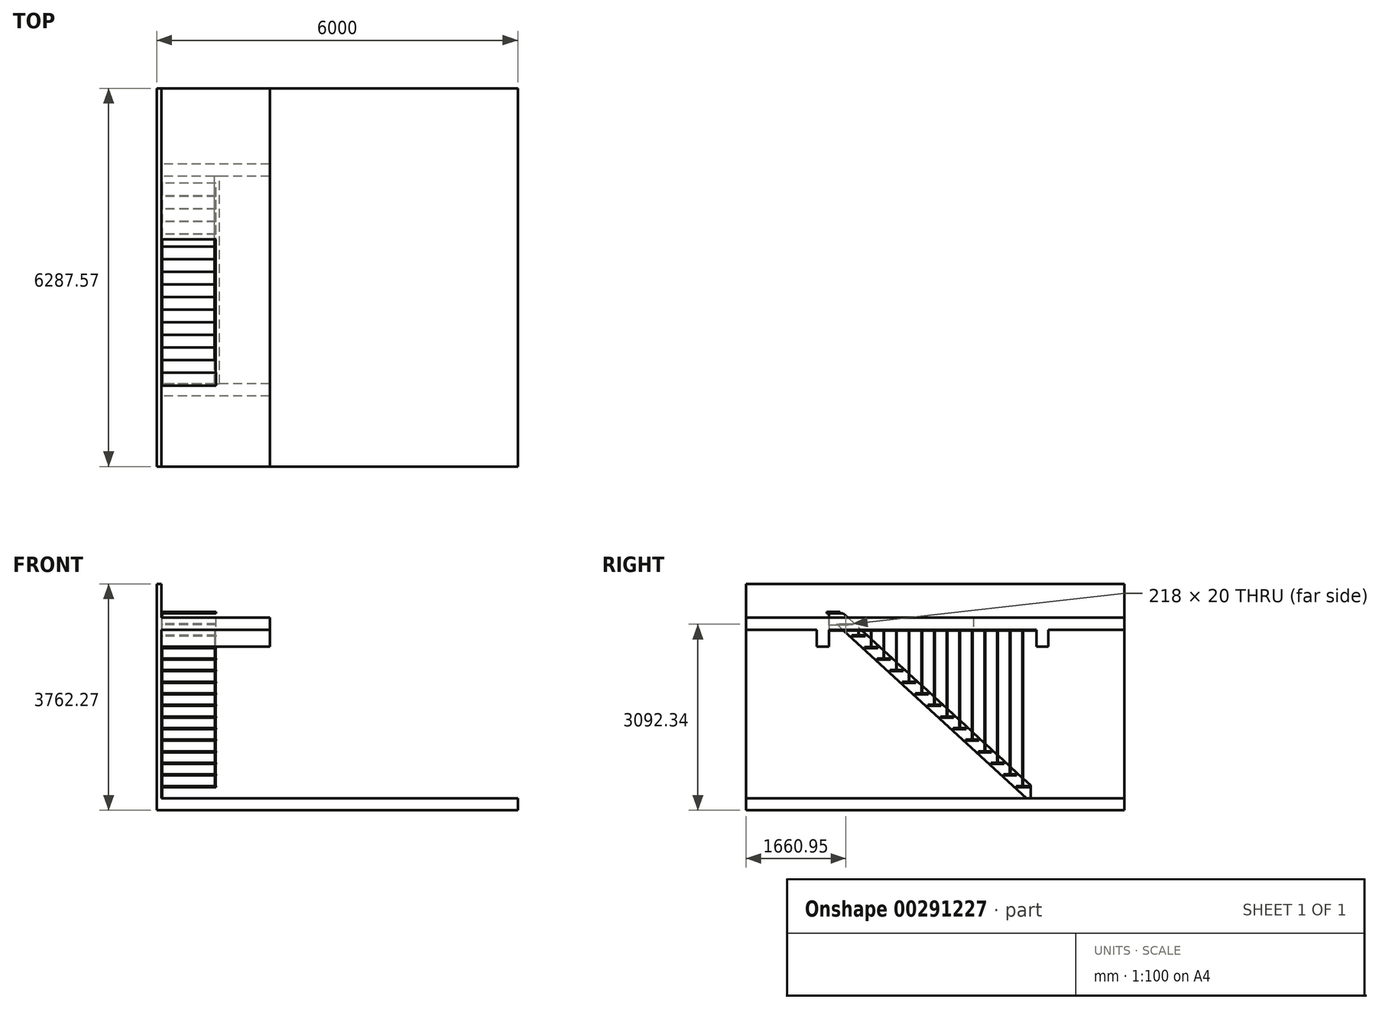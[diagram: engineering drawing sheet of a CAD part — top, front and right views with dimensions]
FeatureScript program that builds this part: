
annotation { "Feature Type Name" : "Feature", "Feature Type Description" : "" }
export const myFeature = defineFeature(function(context is Context, id is Id, definition is map)
    precondition{}
    {
        {
            var Q0;
            Q0=qCreatedBy(makeId("Right.planeOp"),FACE);
            var sketch = newSketch(context, id + "F0", { "sketchPlane" : qUnion([Q0])});
            skLineSegment(sketch, "E0", {"start": v(-3201.03, 2875.04) * mm, "end": v(-3352.23, 2875.04) * mm});
            skLineSegment(sketch, "E1", {"start": v(-3352.23, 2875.04) * mm, "end": v(-3352.23, 3075.04) * mm});
            skLineSegment(sketch, "E2", {"start": v(-3352.23, 3075.04) * mm, "end": v(-3115.13, 3075.04) * mm});
            skLineSegment(sketch, "E3", {"start": v(-3115.13, 3075.04) * mm, "end": v(0, 214.6) * mm});
            skLineSegment(sketch, "E4", {"start": v(0, 214.6) * mm, "end": v(0, 0) * mm});
            skLineSegment(sketch, "E5", {"start": v(0, 0) * mm, "end": v(-70, 0) * mm});
            skLineSegment(sketch, "E6", {"start": v(-70, 0) * mm, "end": v(-3201.03, 2875.04) * mm});
            skSolve(sketch);
        }
        {
            var Q0;
            Q0 = qSketchRegion(id + "F0", true);
            extrude(context, id + "F1", {"entities" : qUnion([Q0]), "depth" : 10 * mm});
        }
        {
            var Q0;
            Q0=qCreatedBy(makeId("Right.planeOp"),FACE);
            var sketch = newSketch(context, id + "F2", { "sketchPlane" : qUnion([Q0])});
            skLineSegment(sketch, "E7.bottom", {"start": v(-4728.97, 3562.27) * mm, "end": v(1558.6, 3562.27) * mm});
            skLineSegment(sketch, "E7.top", {"start": v(-4728.97, 0) * mm, "end": v(1558.6, 0) * mm});
            skLineSegment(sketch, "E7.left", {"start": v(-4728.97, 3562.27) * mm, "end": v(-4728.97, 0) * mm});
            skLineSegment(sketch, "E7.right", {"start": v(1558.6, 3562.27) * mm, "end": v(1558.6, 0) * mm});
            skSolve(sketch);
        }
        {
            var Q0;
            Q0 = qSketchRegion(id + "F2", true);
            extrude(context, id + "F3", {"entities" : qUnion([Q0]), "operationType" : NewBodyOperationType.ADD, "oppositeDirection" : true, "depth" : 80 * mm});
        }
        {
            var Q0;
            Q0=makeQuery(id+"F1.opExtrude","CAP_FACE",FACE,{"disambiguationData":[OSD([sQuery(id+"F0.wireOp",EDGE,"E0"),sQuery(id+"F0.wireOp",EDGE,"E1"),sQuery(id+"F0.wireOp",EDGE,"E2"),sQuery(id+"F0.wireOp",EDGE,"E3"),sQuery(id+"F0.wireOp",EDGE,"E4"),sQuery(id+"F0.wireOp",EDGE,"E5"),sQuery(id+"F0.wireOp",EDGE,"E6")])],"isStart":false});
            var sketch = newSketch(context, id + "F4", { "sketchPlane" : qUnion([Q0])});
            skLineSegment(sketch, "E8", {"start": v(0, 214.6) * mm, "end": v(-138.93, 63.3) * mm, "construction": true});
            skLineSegment(sketch, "E9", {"start": v(-69.47, 138.95) * mm, "end": v(-3158.58, 2975.5) * mm, "construction": true});
            skSolve(sketch);
        }
        {
            var Q0;
            Q0=makeQuery(id+"F4.imprint","IMPRINT",FACE,{"disambiguationData":[TD([[makeQuery(id+"F4.imprint","IMPRINT",EDGE,{"derivedFrom":makeQuery(id+"F1.opExtrude","CAP_EDGE",EDGE,{"disambiguationData":[OSD([sQuery(id+"F0.wireOp",EDGE,"E0")])],"isStart":false})}),-1.0]])]});
            var sketch = newSketch(context, id + "F5", { "sketchPlane" : qUnion([Q0])});
            skLineSegment(sketch, "E10.bottom", {"start": v(-239.07, 204.6) * mm, "end": v(-21.07, 204.6) * mm});
            skLineSegment(sketch, "E10.top", {"start": v(-239.07, 184.6) * mm, "end": v(-21.07, 184.6) * mm});
            skLineSegment(sketch, "E10.left", {"start": v(-239.07, 204.6) * mm, "end": v(-239.07, 184.6) * mm});
            skLineSegment(sketch, "E10.right", {"start": v(-21.07, 204.6) * mm, "end": v(-21.07, 184.6) * mm});
            skLineSegment(sketch, "E11", {"start": v(-130.07, 204.6) * mm, "end": v(-130.07, 184.6) * mm, "construction": true});
            skPoint(sketch, "E12", {"position": v(-130.07, 194.6) * mm});
            skPoint(sketch, "E13.0.1.0", {"position": v(-339.93, 387.3) * mm});
            skLineSegment(sketch, "E13.0.1.1", {"start": v(-448.93, 397.3) * mm, "end": v(-230.93, 397.3) * mm});
            skLineSegment(sketch, "E13.0.1.2", {"start": v(-448.93, 397.3) * mm, "end": v(-448.93, 377.3) * mm});
            skLineSegment(sketch, "E13.0.1.3", {"start": v(-448.93, 377.3) * mm, "end": v(-230.93, 377.3) * mm});
            skLineSegment(sketch, "E13.0.1.4", {"start": v(-230.93, 397.3) * mm, "end": v(-230.93, 377.3) * mm});
            skPoint(sketch, "E13.0.2.0", {"position": v(-549.78, 580) * mm});
            skLineSegment(sketch, "E13.0.2.1", {"start": v(-658.78, 590) * mm, "end": v(-440.78, 590) * mm});
            skLineSegment(sketch, "E13.0.2.2", {"start": v(-658.78, 590) * mm, "end": v(-658.78, 570) * mm});
            skLineSegment(sketch, "E13.0.2.3", {"start": v(-658.78, 570) * mm, "end": v(-440.78, 570) * mm});
            skLineSegment(sketch, "E13.0.2.4", {"start": v(-440.78, 590) * mm, "end": v(-440.78, 570) * mm});
            skPoint(sketch, "E13.0.3.0", {"position": v(-759.63, 772.69) * mm});
            skLineSegment(sketch, "E13.0.3.1", {"start": v(-868.63, 782.69) * mm, "end": v(-650.63, 782.69) * mm});
            skLineSegment(sketch, "E13.0.3.2", {"start": v(-868.63, 782.69) * mm, "end": v(-868.63, 762.69) * mm});
            skLineSegment(sketch, "E13.0.3.3", {"start": v(-868.63, 762.69) * mm, "end": v(-650.63, 762.69) * mm});
            skLineSegment(sketch, "E13.0.3.4", {"start": v(-650.63, 782.69) * mm, "end": v(-650.63, 762.69) * mm});
            skPoint(sketch, "E13.0.4.0", {"position": v(-969.49, 965.38) * mm});
            skLineSegment(sketch, "E13.0.4.1", {"start": v(-1078.49, 975.38) * mm, "end": v(-860.49, 975.38) * mm});
            skLineSegment(sketch, "E13.0.4.2", {"start": v(-1078.49, 975.38) * mm, "end": v(-1078.49, 955.38) * mm});
            skLineSegment(sketch, "E13.0.4.3", {"start": v(-1078.49, 955.38) * mm, "end": v(-860.49, 955.38) * mm});
            skLineSegment(sketch, "E13.0.4.4", {"start": v(-860.49, 975.38) * mm, "end": v(-860.49, 955.38) * mm});
            skPoint(sketch, "E13.0.5.0", {"position": v(-1179.34, 1158.08) * mm});
            skLineSegment(sketch, "E13.0.5.1", {"start": v(-1288.34, 1168.08) * mm, "end": v(-1070.34, 1168.08) * mm});
            skLineSegment(sketch, "E13.0.5.2", {"start": v(-1288.34, 1168.08) * mm, "end": v(-1288.34, 1148.08) * mm});
            skLineSegment(sketch, "E13.0.5.3", {"start": v(-1288.34, 1148.08) * mm, "end": v(-1070.34, 1148.08) * mm});
            skLineSegment(sketch, "E13.0.5.4", {"start": v(-1070.34, 1168.08) * mm, "end": v(-1070.34, 1148.08) * mm});
            skPoint(sketch, "E13.0.6.0", {"position": v(-1389.2, 1350.77) * mm});
            skLineSegment(sketch, "E13.0.6.1", {"start": v(-1498.2, 1360.77) * mm, "end": v(-1280.2, 1360.77) * mm});
            skLineSegment(sketch, "E13.0.6.2", {"start": v(-1498.2, 1360.77) * mm, "end": v(-1498.2, 1340.77) * mm});
            skLineSegment(sketch, "E13.0.6.3", {"start": v(-1498.2, 1340.77) * mm, "end": v(-1280.2, 1340.77) * mm});
            skLineSegment(sketch, "E13.0.6.4", {"start": v(-1280.2, 1360.77) * mm, "end": v(-1280.2, 1340.77) * mm});
            skPoint(sketch, "E13.0.7.0", {"position": v(-1599.05, 1543.47) * mm});
            skLineSegment(sketch, "E13.0.7.1", {"start": v(-1708.05, 1553.47) * mm, "end": v(-1490.05, 1553.47) * mm});
            skLineSegment(sketch, "E13.0.7.2", {"start": v(-1708.05, 1553.47) * mm, "end": v(-1708.05, 1533.47) * mm});
            skLineSegment(sketch, "E13.0.7.3", {"start": v(-1708.05, 1533.47) * mm, "end": v(-1490.05, 1533.47) * mm});
            skLineSegment(sketch, "E13.0.7.4", {"start": v(-1490.05, 1553.47) * mm, "end": v(-1490.05, 1533.47) * mm});
            skPoint(sketch, "E13.0.8.0", {"position": v(-1808.9, 1736.17) * mm});
            skLineSegment(sketch, "E13.0.8.1", {"start": v(-1917.9, 1746.17) * mm, "end": v(-1699.9, 1746.17) * mm});
            skLineSegment(sketch, "E13.0.8.2", {"start": v(-1917.9, 1746.17) * mm, "end": v(-1917.9, 1726.17) * mm});
            skLineSegment(sketch, "E13.0.8.3", {"start": v(-1917.9, 1726.17) * mm, "end": v(-1699.9, 1726.17) * mm});
            skLineSegment(sketch, "E13.0.8.4", {"start": v(-1699.9, 1746.17) * mm, "end": v(-1699.9, 1726.17) * mm});
            skPoint(sketch, "E13.0.9.0", {"position": v(-2018.75, 1928.86) * mm});
            skLineSegment(sketch, "E13.0.9.1", {"start": v(-2127.75, 1938.86) * mm, "end": v(-1909.75, 1938.86) * mm});
            skLineSegment(sketch, "E13.0.9.2", {"start": v(-2127.75, 1938.86) * mm, "end": v(-2127.75, 1918.86) * mm});
            skLineSegment(sketch, "E13.0.9.3", {"start": v(-2127.75, 1918.86) * mm, "end": v(-1909.75, 1918.86) * mm});
            skLineSegment(sketch, "E13.0.9.4", {"start": v(-1909.75, 1938.86) * mm, "end": v(-1909.75, 1918.86) * mm});
            skPoint(sketch, "E13.0.10.0", {"position": v(-2228.6, 2121.56) * mm});
            skLineSegment(sketch, "E13.0.10.1", {"start": v(-2337.6, 2131.56) * mm, "end": v(-2119.6, 2131.56) * mm});
            skLineSegment(sketch, "E13.0.10.2", {"start": v(-2337.6, 2131.56) * mm, "end": v(-2337.6, 2111.56) * mm});
            skLineSegment(sketch, "E13.0.10.3", {"start": v(-2337.6, 2111.56) * mm, "end": v(-2119.6, 2111.56) * mm});
            skLineSegment(sketch, "E13.0.10.4", {"start": v(-2119.6, 2131.56) * mm, "end": v(-2119.6, 2111.56) * mm});
            skPoint(sketch, "E13.0.11.0", {"position": v(-2438.46, 2314.25) * mm});
            skLineSegment(sketch, "E13.0.11.1", {"start": v(-2547.46, 2324.25) * mm, "end": v(-2329.46, 2324.25) * mm});
            skLineSegment(sketch, "E13.0.11.2", {"start": v(-2547.46, 2324.25) * mm, "end": v(-2547.46, 2304.25) * mm});
            skLineSegment(sketch, "E13.0.11.3", {"start": v(-2547.46, 2304.25) * mm, "end": v(-2329.46, 2304.25) * mm});
            skLineSegment(sketch, "E13.0.11.4", {"start": v(-2329.46, 2324.25) * mm, "end": v(-2329.46, 2304.25) * mm});
            skPoint(sketch, "E13.0.12.0", {"position": v(-2648.32, 2506.95) * mm});
            skLineSegment(sketch, "E13.0.12.1", {"start": v(-2757.32, 2516.95) * mm, "end": v(-2539.32, 2516.95) * mm});
            skLineSegment(sketch, "E13.0.12.2", {"start": v(-2757.32, 2516.95) * mm, "end": v(-2757.32, 2496.95) * mm});
            skLineSegment(sketch, "E13.0.12.3", {"start": v(-2757.32, 2496.95) * mm, "end": v(-2539.32, 2496.95) * mm});
            skLineSegment(sketch, "E13.0.12.4", {"start": v(-2539.32, 2516.95) * mm, "end": v(-2539.32, 2496.95) * mm});
            skPoint(sketch, "E13.0.13.0", {"position": v(-2858.17, 2699.64) * mm});
            skLineSegment(sketch, "E13.0.13.1", {"start": v(-2967.17, 2709.64) * mm, "end": v(-2749.17, 2709.64) * mm});
            skLineSegment(sketch, "E13.0.13.2", {"start": v(-2967.17, 2709.64) * mm, "end": v(-2967.17, 2689.64) * mm});
            skLineSegment(sketch, "E13.0.13.3", {"start": v(-2967.17, 2689.64) * mm, "end": v(-2749.17, 2689.64) * mm});
            skLineSegment(sketch, "E13.0.13.4", {"start": v(-2749.17, 2709.64) * mm, "end": v(-2749.17, 2689.64) * mm});
            skPoint(sketch, "E13.0.14.0", {"position": v(-3068.02, 2892.34) * mm});
            skLineSegment(sketch, "E13.0.14.1", {"start": v(-3177.02, 2902.34) * mm, "end": v(-2959.02, 2902.34) * mm});
            skLineSegment(sketch, "E13.0.14.2", {"start": v(-3177.02, 2902.34) * mm, "end": v(-3177.02, 2882.34) * mm});
            skLineSegment(sketch, "E13.0.14.3", {"start": v(-3177.02, 2882.34) * mm, "end": v(-2959.02, 2882.34) * mm});
            skLineSegment(sketch, "E13.0.14.4", {"start": v(-2959.02, 2902.34) * mm, "end": v(-2959.02, 2882.34) * mm});
            skPoint(sketch, "E13.0.15.0", {"position": v(-3277.88, 3085.04) * mm});
            skLineSegment(sketch, "E13.0.15.1", {"start": v(-3386.88, 3095.04) * mm, "end": v(-3168.88, 3095.04) * mm});
            skLineSegment(sketch, "E13.0.15.2", {"start": v(-3386.88, 3095.04) * mm, "end": v(-3386.88, 3075.04) * mm});
            skLineSegment(sketch, "E13.0.15.3", {"start": v(-3386.88, 3075.04) * mm, "end": v(-3168.88, 3075.04) * mm});
            skLineSegment(sketch, "E13.0.15.4", {"start": v(-3168.88, 3095.04) * mm, "end": v(-3168.88, 3075.04) * mm});
            skLineSegment(sketch, "E13.direction1", {"start": v(-130.07, 194.6) * mm, "end": v(-105.07, 194.6) * mm, "construction": true});
            skLineSegment(sketch, "E13.direction2", {"start": v(-130.07, 194.6) * mm, "end": v(-339.93, 387.3) * mm, "construction": true});
            skSolve(sketch);
        }
        {
            var Q0;
            Q0 = qSketchRegion(id + "F5", true);
            extrude(context, id + "F6", {"entities" : qUnion([Q0]), "operationType" : NewBodyOperationType.ADD, "depth" : 895.5 * mm});
        }
        {
            var Q0;
            Q0=makeQuery(id+"F3.opExtrude","CAP_FACE",FACE,{"disambiguationData":[OSD([sQuery(id+"F2.wireOp",EDGE,"E7.bottom"),sQuery(id+"F2.wireOp",EDGE,"E7.top"),sQuery(id+"F2.wireOp",EDGE,"E7.left"),sQuery(id+"F2.wireOp",EDGE,"E7.right")])],"isStart":true});
            var sketch = newSketch(context, id + "F7", { "sketchPlane" : qUnion([Q0])});
            skLineSegment(sketch, "E14", {"start": v(-4728.97, 3000) * mm, "end": v(-3352.23, 3000) * mm});
            skLineSegment(sketch, "E15", {"start": v(-3552.23, 2800) * mm, "end": v(-4728.97, 2800) * mm});
            skLineSegment(sketch, "E16", {"start": v(-4728.97, 2800) * mm, "end": v(-4728.97, 3000) * mm});
            skLineSegment(sketch, "E17", {"start": v(-952.23, 3000) * mm, "end": v(-952.23, 2800) * mm});
            skLineSegment(sketch, "E18", {"start": v(-952.23, 2800) * mm, "end": v(97.77, 2800) * mm});
            skLineSegment(sketch, "E19", {"start": v(97.77, 2800) * mm, "end": v(97.77, 2520) * mm});
            skLineSegment(sketch, "E20", {"start": v(97.77, 2520) * mm, "end": v(297.77, 2520) * mm});
            skLineSegment(sketch, "E21", {"start": v(297.77, 2520) * mm, "end": v(297.77, 2800) * mm});
            skLineSegment(sketch, "E22", {"start": v(297.77, 2800) * mm, "end": v(1558.6, 2800) * mm});
            skLineSegment(sketch, "E23", {"start": v(1558.6, 2800) * mm, "end": v(1558.6, 3000) * mm});
            skLineSegment(sketch, "E24", {"start": v(1558.6, 3000) * mm, "end": v(-952.23, 3000) * mm});
            skLineSegment(sketch, "E25", {"start": v(-3352.23, 3000) * mm, "end": v(-3352.23, 2520) * mm});
            skLineSegment(sketch, "E26", {"start": v(-3352.23, 2520) * mm, "end": v(-3552.23, 2520) * mm});
            skLineSegment(sketch, "E27", {"start": v(-3552.23, 2520) * mm, "end": v(-3552.23, 2800) * mm});
            skSolve(sketch);
        }
        {
            var Q0;
            Q0 = qSketchRegion(id + "F7", true);
            extrude(context, id + "F8", {"entities" : qUnion([Q0]), "operationType" : NewBodyOperationType.ADD, "depth" : 900 * mm});
        }
        {
            var Q0;
            Q0=makeQuery(id+"F8.opExtrude","CAP_FACE",FACE,{"disambiguationData":[OSD([sQuery(id+"F7.wireOp",EDGE,"E14"),sQuery(id+"F7.wireOp",EDGE,"E15"),sQuery(id+"F7.wireOp",EDGE,"E16"),sQuery(id+"F7.wireOp",EDGE,"E25"),sQuery(id+"F7.wireOp",EDGE,"E26"),sQuery(id+"F7.wireOp",EDGE,"E27")])],"isStart":false});
            var sketch = newSketch(context, id + "F9", { "sketchPlane" : qUnion([Q0])});
            skLineSegment(sketch, "E28", {"start": v(-4728.97, 3000) * mm, "end": v(1558.6, 3000) * mm});
            skLineSegment(sketch, "E29", {"start": v(1558.6, 3000) * mm, "end": v(1558.6, 2800) * mm});
            skLineSegment(sketch, "E30", {"start": v(1558.6, 2800) * mm, "end": v(297.77, 2800) * mm});
            skLineSegment(sketch, "E31", {"start": v(297.77, 2800) * mm, "end": v(297.77, 2520) * mm});
            skLineSegment(sketch, "E32", {"start": v(297.77, 2520) * mm, "end": v(97.77, 2520) * mm});
            skLineSegment(sketch, "E33", {"start": v(97.77, 2520) * mm, "end": v(97.77, 2800) * mm});
            skLineSegment(sketch, "E34", {"start": v(97.77, 2800) * mm, "end": v(-3352.23, 2800) * mm});
            skLineSegment(sketch, "E35", {"start": v(-3352.23, 2800) * mm, "end": v(-3352.23, 2520) * mm});
            skLineSegment(sketch, "E36", {"start": v(-3352.23, 2520) * mm, "end": v(-3552.23, 2520) * mm});
            skLineSegment(sketch, "E37", {"start": v(-3552.23, 2520) * mm, "end": v(-3552.23, 2800) * mm});
            skLineSegment(sketch, "E38", {"start": v(-3552.23, 2800) * mm, "end": v(-4728.97, 2800) * mm});
            skLineSegment(sketch, "E39", {"start": v(-4728.97, 2800) * mm, "end": v(-4728.97, 3000) * mm});
            skSolve(sketch);
        }
        {
            var Q0;
            Q0 = qSketchRegion(id + "F9", true);
            extrude(context, id + "F10", {"entities" : qUnion([Q0]), "operationType" : NewBodyOperationType.ADD, "depth" : 900 * mm});
        }
        {
            var Q0;
            Q0=makeQuery(id+"F10.boolean.opBoolean","MERGE",FACE,{"derivedFrom":[makeQuery(id+"F8.opExtrude","SWEPT_FACE",FACE,{"disambiguationData":[OSD([sQuery(id+"F7.wireOp",EDGE,"E18")])]}),makeQuery(id+"F10.opExtrude","SWEPT_FACE",FACE,{"disambiguationData":[OSD([sQuery(id+"F9.wireOp",EDGE,"E34")])]})]});
            var sketch = newSketch(context, id + "F11", { "sketchPlane" : qUnion([Q0])});
            skLineSegment(sketch, "E40.bottom", {"start": v(880, 3352.23) * mm, "end": v(960, 3352.23) * mm});
            skLineSegment(sketch, "E40.top", {"start": v(880, -97.77) * mm, "end": v(960, -97.77) * mm});
            skLineSegment(sketch, "E40.left", {"start": v(880, 3352.23) * mm, "end": v(880, -97.77) * mm});
            skLineSegment(sketch, "E40.right", {"start": v(960, 3352.23) * mm, "end": v(960, -97.77) * mm});
            skSolve(sketch);
        }
        {
            var Q0;
            Q0 = qSketchRegion(id + "F11", true);
            extrude(context, id + "F12", {"entities" : qUnion([Q0]), "operationType" : NewBodyOperationType.ADD, "depth" : 10 * mm});
        }
        {
            var Q0;
            Q0=makeQuery(id+"F12.opExtrude","CAP_FACE",FACE,{"disambiguationData":[OSD([sQuery(id+"F11.wireOp",EDGE,"E40.bottom"),sQuery(id+"F11.wireOp",EDGE,"E40.top"),sQuery(id+"F11.wireOp",EDGE,"E40.left"),sQuery(id+"F11.wireOp",EDGE,"E40.right")])],"isStart":false});
            var sketch = newSketch(context, id + "F13", { "sketchPlane" : qUnion([Q0])});
            skLineSegment(sketch, "E41", {"start": v(880, 2858.17) * mm, "end": v(905.5, 2858.17) * mm, "construction": true});
            skLineSegment(sketch, "E42", {"start": v(892.75, 2858.17) * mm, "end": v(892.75, -97.77) * mm, "construction": true});
            skCircle(sketch, "E43", {"center": v(892.75, 2858.17) * mm, "radius": 5 * mm});
            skLineSegment(sketch, "E44", {"start": v(880, 130.07) * mm, "end": v(892.75, 130.07) * mm, "construction": true});
            skCircle(sketch, "E45.0.1.0", {"center": v(892.75, 2648.32) * mm, "radius": 5 * mm});
            skCircle(sketch, "E45.0.2.0", {"center": v(892.75, 2438.46) * mm, "radius": 5 * mm});
            skCircle(sketch, "E45.0.3.0", {"center": v(892.75, 2228.6) * mm, "radius": 5 * mm});
            skCircle(sketch, "E45.0.4.0", {"center": v(892.75, 2018.75) * mm, "radius": 5 * mm});
            skCircle(sketch, "E45.0.5.0", {"center": v(892.75, 1808.9) * mm, "radius": 5 * mm});
            skCircle(sketch, "E45.0.6.0", {"center": v(892.75, 1599.05) * mm, "radius": 5 * mm});
            skCircle(sketch, "E45.0.7.0", {"center": v(892.75, 1389.2) * mm, "radius": 5 * mm});
            skCircle(sketch, "E45.0.8.0", {"center": v(892.75, 1179.34) * mm, "radius": 5 * mm});
            skCircle(sketch, "E45.0.9.0", {"center": v(892.75, 969.49) * mm, "radius": 5 * mm});
            skCircle(sketch, "E45.0.10.0", {"center": v(892.75, 759.63) * mm, "radius": 5 * mm});
            skCircle(sketch, "E45.0.11.0", {"center": v(892.75, 549.78) * mm, "radius": 5 * mm});
            skCircle(sketch, "E45.0.12.0", {"center": v(892.75, 339.93) * mm, "radius": 5 * mm});
            skCircle(sketch, "E45.0.13.0", {"center": v(892.75, 130.07) * mm, "radius": 5 * mm});
            skLineSegment(sketch, "E45.direction1", {"start": v(892.75, 2858.17) * mm, "end": v(917.75, 2858.17) * mm, "construction": true});
            skLineSegment(sketch, "E45.direction2", {"start": v(892.75, 2858.17) * mm, "end": v(892.75, 2648.32) * mm, "construction": true});
            skSolve(sketch);
        }
        {
            var Q0;
            Q0 = qSketchRegion(id + "F13", true);
            extrude(context, id + "F14", {"entities" : qUnion([Q0]), "operationType" : NewBodyOperationType.ADD, "endBound" : BoundingType.UP_TO_NEXT, "depth" : 25 * mm});
        }
        {
            var Q0;
            Q0=makeQuery(id+"F3.opExtrude","CAP_FACE",FACE,{"disambiguationData":[OSD([sQuery(id+"F2.wireOp",EDGE,"E7.bottom"),sQuery(id+"F2.wireOp",EDGE,"E7.top"),sQuery(id+"F2.wireOp",EDGE,"E7.left"),sQuery(id+"F2.wireOp",EDGE,"E7.right")])],"isStart":false});
            var sketch = newSketch(context, id + "F15", { "sketchPlane" : qUnion([Q0])});
            skLineSegment(sketch, "E46.bottom", {"start": v(4728.97, 0) * mm, "end": v(-1558.6, 0) * mm});
            skLineSegment(sketch, "E46.top", {"start": v(4728.97, -200) * mm, "end": v(-1558.6, -200) * mm});
            skLineSegment(sketch, "E46.left", {"start": v(4728.97, 0) * mm, "end": v(4728.97, -200) * mm});
            skLineSegment(sketch, "E46.right", {"start": v(-1558.6, 0) * mm, "end": v(-1558.6, -200) * mm});
            skSolve(sketch);
        }
        {
            var Q0;
            Q0 = qSketchRegion(id + "F15", true);
            var Q1;
            Q1=makeQuery(id+"F10.opExtrude","CAP_FACE",FACE,{"disambiguationData":[OSD([sQuery(id+"F9.wireOp",EDGE,"E28"),sQuery(id+"F9.wireOp",EDGE,"E29"),sQuery(id+"F9.wireOp",EDGE,"E30"),sQuery(id+"F9.wireOp",EDGE,"E31"),sQuery(id+"F9.wireOp",EDGE,"E32"),sQuery(id+"F9.wireOp",EDGE,"E33"),sQuery(id+"F9.wireOp",EDGE,"E34"),sQuery(id+"F9.wireOp",EDGE,"E35"),sQuery(id+"F9.wireOp",EDGE,"E36"),sQuery(id+"F9.wireOp",EDGE,"E37"),sQuery(id+"F9.wireOp",EDGE,"E38"),sQuery(id+"F9.wireOp",EDGE,"E39")])],"isStart":false});
            extrude(context, id + "F16", {"entities" : qUnion([Q0]), "operationType" : NewBodyOperationType.ADD, "oppositeDirection" : true, "endBoundEntityFace" : qUnion([Q1]), "depth" : 6000 * mm});
        }
    });
